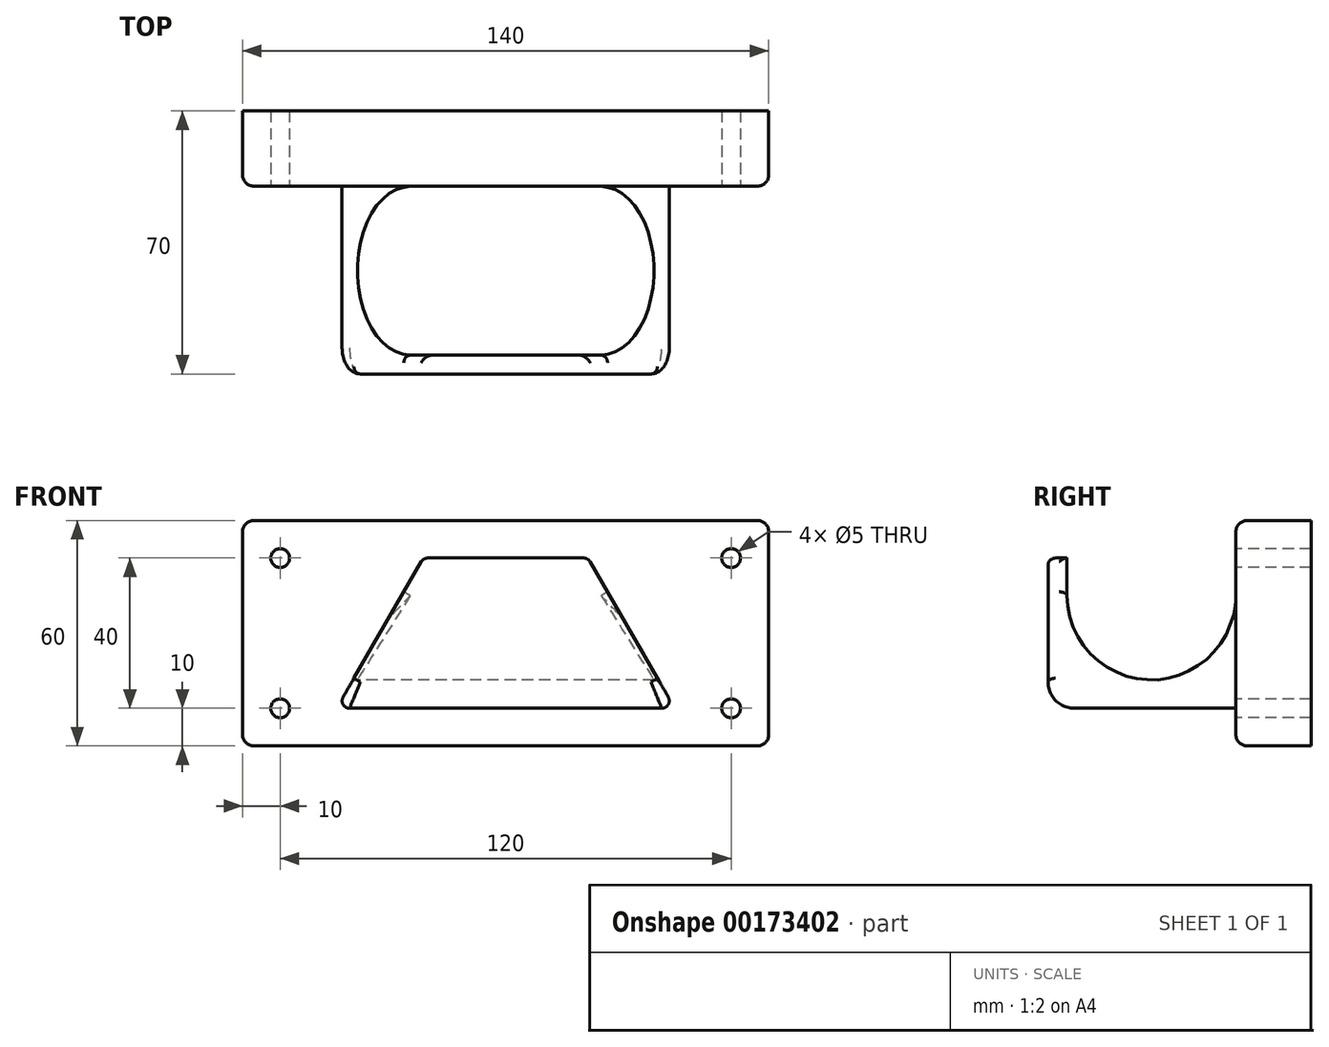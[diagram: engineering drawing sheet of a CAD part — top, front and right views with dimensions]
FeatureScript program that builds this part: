
annotation { "Feature Type Name" : "Feature", "Feature Type Description" : "" }
export const myFeature = defineFeature(function(context is Context, id is Id, definition is map)
    precondition{}
    {
        {
            var Q0;
            Q0=qCreatedBy(makeId("Front.planeOp"),FACE);
            var sketch = newSketch(context, id + "F0", { "sketchPlane" : qUnion([Q0])});
            skLineSegment(sketch, "E0.bottom", {"start": v(0, 0) * mm, "end": v(140, 0) * mm});
            skLineSegment(sketch, "E0.top", {"start": v(0, 60) * mm, "end": v(140, 60) * mm});
            skLineSegment(sketch, "E0.left", {"start": v(0, 0) * mm, "end": v(0, 60) * mm});
            skLineSegment(sketch, "E0.right", {"start": v(140, 0) * mm, "end": v(140, 60) * mm});
            skSolve(sketch);
        }
        {
            var Q0;
            Q0=makeQuery(id+"F0.imprint","IMPRINT",FACE,{"disambiguationData":[TD([[makeQuery(id+"F0.imprint","IMPRINT",EDGE,{"derivedFrom":sQuery(id+"F0.wireOp",EDGE,"E0.bottom")}),1.0]])]});
            extrude(context, id + "F1", {"entities" : qUnion([Q0]), "depth" : 20 * mm});
        }
        {
            var Q0;
            Q0=makeQuery(id+"F1.opExtrude","CAP_FACE",FACE,{"disambiguationData":[OSD([sQuery(id+"F0.wireOp",EDGE,"E0.bottom"),sQuery(id+"F0.wireOp",EDGE,"E0.top"),sQuery(id+"F0.wireOp",EDGE,"E0.left"),sQuery(id+"F0.wireOp",EDGE,"E0.right")])],"isStart":false});
            var sketch = newSketch(context, id + "F2", { "sketchPlane" : qUnion([Q0])});
            skLineSegment(sketch, "E1", {"start": v(25, 10) * mm, "end": v(115, 10) * mm});
            skLineSegment(sketch, "E2", {"start": v(115, 10) * mm, "end": v(91.9, 50) * mm});
            skLineSegment(sketch, "E3", {"start": v(91.9, 50) * mm, "end": v(48.1, 50) * mm});
            skLineSegment(sketch, "E4", {"start": v(48.1, 50) * mm, "end": v(25, 10) * mm});
            skSolve(sketch);
        }
        {
            var Q0;
            Q0=makeQuery(id+"F2.imprint","IMPRINT",FACE,{"disambiguationData":[TD([[makeQuery(id+"F2.imprint","IMPRINT",EDGE,{"derivedFrom":sQuery(id+"F2.wireOp",EDGE,"E1")}),1.0]])]});
            extrude(context, id + "F3", {"entities" : qUnion([Q0]), "operationType" : NewBodyOperationType.ADD, "depth" : 50 * mm});
        }
        {
            var Q0;
            Q0=qCreatedBy(makeId("Right.planeOp"),FACE);
            var sketch = newSketch(context, id + "F4", { "sketchPlane" : qUnion([Q0])});
            skLineSegment(sketch, "E5", {"start": v(-65, 40) * mm, "end": v(-65, 50) * mm});
            skLineSegment(sketch, "E6", {"start": v(-20, 40) * mm, "end": v(-20, 50) * mm});
            skArc(sketch, "E7", {"start": v(-65, 40) * mm, "mid": v(-42.5, 17.5) * mm, "end": v(-20, 40) * mm});
            skLineSegment(sketch, "E8", {"start": v(-65, 50) * mm, "end": v(-20, 50) * mm});
            skSolve(sketch);
        }
        {
            var Q0;
            Q0 = qSketchRegion(id + "F4", true);
            extrude(context, id + "F5", {"entities" : qUnion([Q0]), "operationType" : NewBodyOperationType.REMOVE, "endBound" : BoundingType.THROUGH_ALL, "depth" : 25 * mm});
        }
        {
            var Q0;
            Q0=makeQuery(id+"F5.boolean.opBoolean","MERGE",FACE,{"derivedFrom":[makeQuery(id+"F1.opExtrude","CAP_FACE",FACE,{"disambiguationData":[OSD([sQuery(id+"F0.wireOp",EDGE,"E0.bottom"),sQuery(id+"F0.wireOp",EDGE,"E0.top"),sQuery(id+"F0.wireOp",EDGE,"E0.left"),sQuery(id+"F0.wireOp",EDGE,"E0.right")])],"isStart":false}),makeQuery(id+"F5.opExtrude","SWEPT_FACE",FACE,{"disambiguationData":[OSD([sQuery(id+"F4.wireOp",EDGE,"E6")])]})]});
            var sketch = newSketch(context, id + "F6", { "sketchPlane" : qUnion([Q0])});
            skCircle(sketch, "E9", {"center": v(10, 50) * mm, "radius": 2.5 * mm});
            skCircle(sketch, "E10", {"center": v(10, 10) * mm, "radius": 2.5 * mm});
            skCircle(sketch, "E11", {"center": v(130, 10) * mm, "radius": 2.5 * mm});
            skCircle(sketch, "E12", {"center": v(130, 50) * mm, "radius": 2.5 * mm});
            skSolve(sketch);
        }
        {
            var Q0;
            Q0 = qSketchRegion(id + "F6", true);
            extrude(context, id + "F7", {"entities" : qUnion([Q0]), "operationType" : NewBodyOperationType.REMOVE, "endBound" : BoundingType.THROUGH_ALL, "oppositeDirection" : true, "depth" : 25 * mm});
        }
        {
            var Q0;
            Q0=makeQuery(id+"F3.opExtrude","CAP_EDGE",EDGE,{"disambiguationData":[OSD([sQuery(id+"F2.wireOp",EDGE,"E4")])],"isStart":true});
            var Q1;
            Q1=makeQuery(id+"F3.opExtrude","CAP_EDGE",EDGE,{"disambiguationData":[OSD([sQuery(id+"F2.wireOp",EDGE,"E1")])],"isStart":true});
            var Q2;
            Q2=makeQuery(id+"F3.opExtrude","SWEPT_EDGE",EDGE,{"disambiguationData":[OSD([sQuery(id+"F2.wireOp",EDGE,"E1"),sQuery(id+"F2.wireOp",EDGE,"E4")])]});
            var Q3;
            Q3=makeQuery(id+"F3.opExtrude","CAP_EDGE",EDGE,{"disambiguationData":[OSD([sQuery(id+"F2.wireOp",EDGE,"E4")])],"isStart":false});
            var Q4;
            Q4=makeQuery(id+"F5.boolean.opBoolean","INTERSECT",EDGE,{"derivedFrom":[makeQuery(id+"F3.opExtrude","SWEPT_FACE",FACE,{"disambiguationData":[OSD([sQuery(id+"F2.wireOp",EDGE,"E4")])]}),makeQuery(id+"F5.opExtrude","SWEPT_FACE",FACE,{"disambiguationData":[OSD([sQuery(id+"F4.wireOp",EDGE,"E7")])]})]});
            var Q5;
            Q5=makeQuery(id+"F5.boolean.opBoolean","COPY",EDGE,{"derivedFrom":makeQuery(id+"F5.opExtrude","SWEPT_EDGE",EDGE,{"disambiguationData":[OSD([sQuery(id+"F4.wireOp",EDGE,"E5"),sQuery(id+"F4.wireOp",EDGE,"E8")])]})});
            var Q6;
            Q6=makeQuery(id+"F5.boolean.opBoolean","INTERSECT",EDGE,{"derivedFrom":[makeQuery(id+"F3.opExtrude","SWEPT_FACE",FACE,{"disambiguationData":[OSD([sQuery(id+"F2.wireOp",EDGE,"E2")])]}),makeQuery(id+"F5.opExtrude","SWEPT_FACE",FACE,{"disambiguationData":[OSD([sQuery(id+"F4.wireOp",EDGE,"E7")])]})]});
            var Q7;
            Q7=makeQuery(id+"F3.opExtrude","SWEPT_EDGE",EDGE,{"disambiguationData":[OSD([sQuery(id+"F2.wireOp",EDGE,"E2"),sQuery(id+"F2.wireOp",EDGE,"E3")])]});
            var Q8;
            Q8=makeQuery(id+"F5.boolean.opBoolean","INTERSECT",EDGE,{"derivedFrom":[makeQuery(id+"F3.opExtrude","SWEPT_FACE",FACE,{"disambiguationData":[OSD([sQuery(id+"F2.wireOp",EDGE,"E2")])]}),makeQuery(id+"F5.opExtrude","SWEPT_FACE",FACE,{"disambiguationData":[OSD([sQuery(id+"F4.wireOp",EDGE,"E5")])]})]});
            var Q9;
            Q9=makeQuery(id+"F5.boolean.opBoolean","INTERSECT",EDGE,{"derivedFrom":[makeQuery(id+"F3.opExtrude","SWEPT_FACE",FACE,{"disambiguationData":[OSD([sQuery(id+"F2.wireOp",EDGE,"E4")])]}),makeQuery(id+"F5.opExtrude","SWEPT_FACE",FACE,{"disambiguationData":[OSD([sQuery(id+"F4.wireOp",EDGE,"E5")])]})]});
            var Q10;
            Q10=makeQuery(id+"F3.opExtrude","SWEPT_EDGE",EDGE,{"disambiguationData":[OSD([sQuery(id+"F2.wireOp",EDGE,"E3"),sQuery(id+"F2.wireOp",EDGE,"E4")])]});
            var Q11;
            Q11=makeQuery(id+"F3.opExtrude","CAP_EDGE",EDGE,{"disambiguationData":[OSD([sQuery(id+"F2.wireOp",EDGE,"E3")])],"isStart":false});
            var Q12;
            Q12=makeQuery(id+"F3.opExtrude","CAP_EDGE",EDGE,{"disambiguationData":[OSD([sQuery(id+"F2.wireOp",EDGE,"E2")])],"isStart":false});
            var Q13;
            Q13=makeQuery(id+"F3.opExtrude","SWEPT_EDGE",EDGE,{"disambiguationData":[OSD([sQuery(id+"F2.wireOp",EDGE,"E1"),sQuery(id+"F2.wireOp",EDGE,"E2")])]});
            var Q14;
            Q14=makeQuery(id+"F3.opExtrude","CAP_EDGE",EDGE,{"disambiguationData":[OSD([sQuery(id+"F2.wireOp",EDGE,"E2")])],"isStart":true});
            fillet(context, id + "F8", {"entities" : qUnion([Q0, Q1, Q2, Q3, Q4, Q5, Q6, Q7, Q8, Q9, Q10, Q11, Q12, Q13, Q14]), "radius" : 2 * mm, "tangentPropagation" : true, "allowEdgeOverflow" : false});
        }
        {
            var Q0;
            Q0=makeQuery(id+"F3.opExtrude","CAP_EDGE",EDGE,{"disambiguationData":[OSD([sQuery(id+"F2.wireOp",EDGE,"E1")])],"isStart":false});
            fillet(context, id + "F9", {"entities" : qUnion([Q0]), "radius" : 7 * mm, "tangentPropagation" : true, "allowEdgeOverflow" : false});
        }
        {
            var Q0;
            Q0=makeQuery(id+"F1.opExtrude","CAP_EDGE",EDGE,{"disambiguationData":[OSD([sQuery(id+"F0.wireOp",EDGE,"E0.left")])],"isStart":false});
            var Q1;
            Q1=makeQuery(id+"F1.opExtrude","SWEPT_EDGE",EDGE,{"disambiguationData":[OSD([sQuery(id+"F0.wireOp",EDGE,"E0.bottom"),sQuery(id+"F0.wireOp",EDGE,"E0.left")])]});
            var Q2;
            Q2=makeQuery(id+"F1.opExtrude","CAP_EDGE",EDGE,{"disambiguationData":[OSD([sQuery(id+"F0.wireOp",EDGE,"E0.bottom")])],"isStart":false});
            var Q3;
            Q3=makeQuery(id+"F1.opExtrude","SWEPT_EDGE",EDGE,{"disambiguationData":[OSD([sQuery(id+"F0.wireOp",EDGE,"E0.bottom"),sQuery(id+"F0.wireOp",EDGE,"E0.right")])]});
            var Q4;
            Q4=makeQuery(id+"F1.opExtrude","CAP_EDGE",EDGE,{"disambiguationData":[OSD([sQuery(id+"F0.wireOp",EDGE,"E0.right")])],"isStart":false});
            var Q5;
            Q5=makeQuery(id+"F1.opExtrude","SWEPT_EDGE",EDGE,{"disambiguationData":[OSD([sQuery(id+"F0.wireOp",EDGE,"E0.top"),sQuery(id+"F0.wireOp",EDGE,"E0.right")])]});
            var Q6;
            Q6=makeQuery(id+"F1.opExtrude","CAP_EDGE",EDGE,{"disambiguationData":[OSD([sQuery(id+"F0.wireOp",EDGE,"E0.top")])],"isStart":false});
            var Q7;
            Q7=makeQuery(id+"F1.opExtrude","SWEPT_EDGE",EDGE,{"disambiguationData":[OSD([sQuery(id+"F0.wireOp",EDGE,"E0.top"),sQuery(id+"F0.wireOp",EDGE,"E0.left")])]});
            fillet(context, id + "F10", {"entities" : qUnion([Q0, Q1, Q2, Q3, Q4, Q5, Q6, Q7]), "radius" : 3 * mm, "tangentPropagation" : true, "allowEdgeOverflow" : false});
        }
    });
